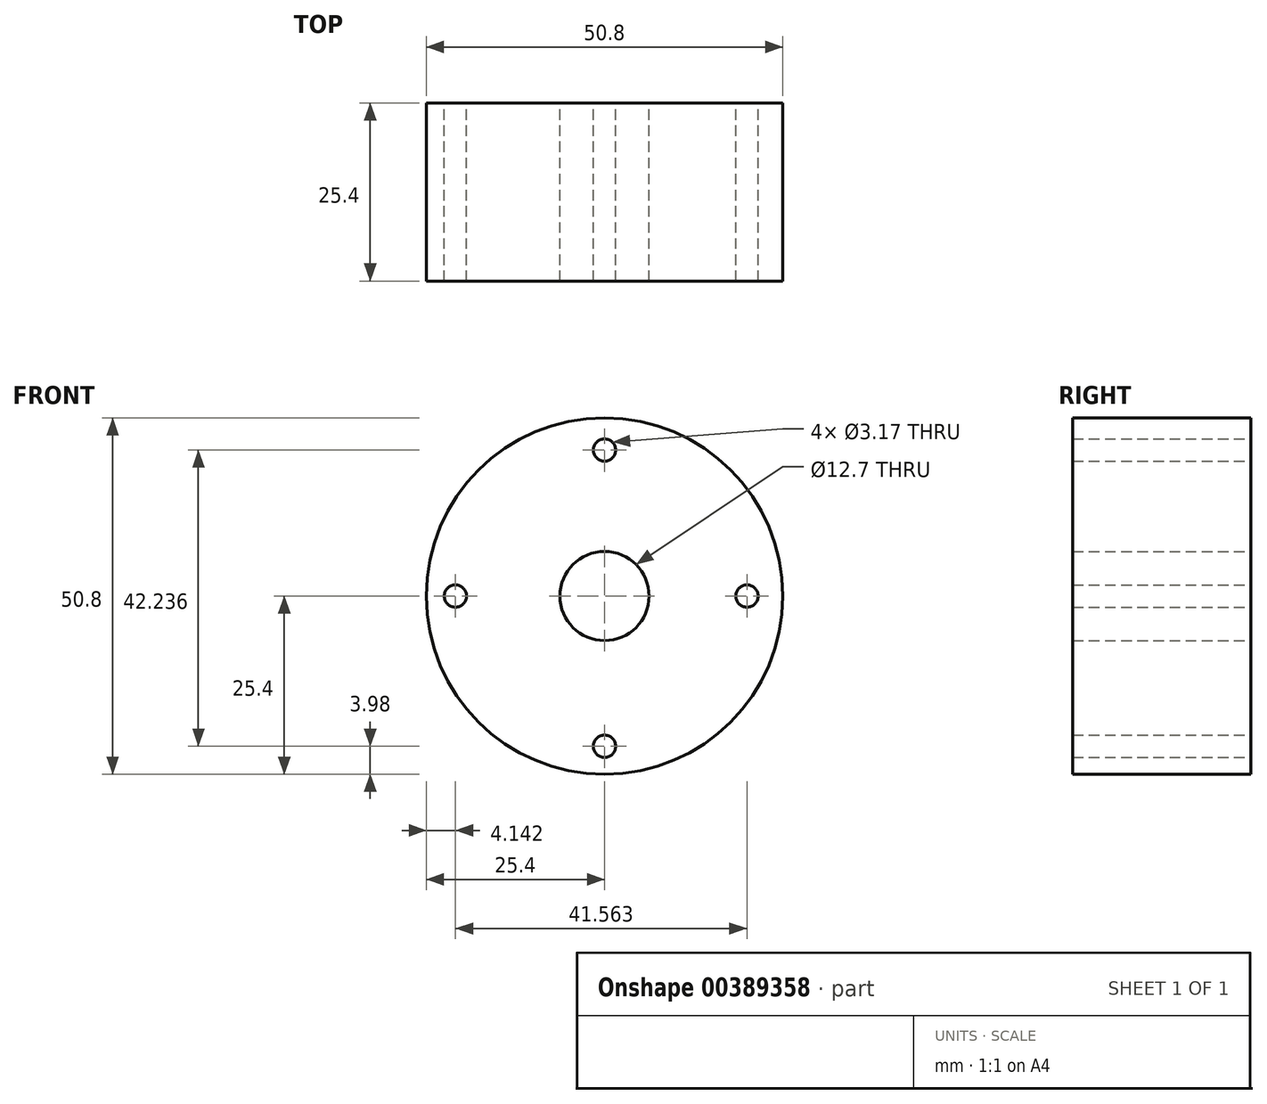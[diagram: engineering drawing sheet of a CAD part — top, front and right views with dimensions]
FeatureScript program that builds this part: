
annotation { "Feature Type Name" : "Feature", "Feature Type Description" : "" }
export const myFeature = defineFeature(function(context is Context, id is Id, definition is map)
    precondition{}
    {
        {
            var Q0;
            Q0=qCreatedBy(makeId("Front.planeOp"),FACE);
            var sketch = newSketch(context, id + "F0", { "sketchPlane" : qUnion([Q0])});
            skCircle(sketch, "E0", {"center": v(0, 0) * mm, "radius": 25.4 * mm});
            skCircle(sketch, "E1", {"center": v(0, 0) * mm, "radius": 22.23 * mm, "construction": true});
            skCircle(sketch, "E2", {"center": v(0, 0) * mm, "radius": 6.35 * mm});
            skCircle(sketch, "E3", {"center": v(0, 20.82) * mm, "radius": 1.59 * mm});
            skCircle(sketch, "E4", {"center": v(0, -21.42) * mm, "radius": 1.59 * mm});
            skCircle(sketch, "E5", {"center": v(-21.26, 0) * mm, "radius": 1.59 * mm});
            skCircle(sketch, "E6", {"center": v(20.3, 0) * mm, "radius": 1.59 * mm});
            skSolve(sketch);
        }
        {
            var Q0;
            Q0 = qSketchRegion(id + "F0", true);
            extrude(context, id + "F1", {"entities" : qUnion([Q0]), "depth" : 25.4 * mm});
        }
    });
